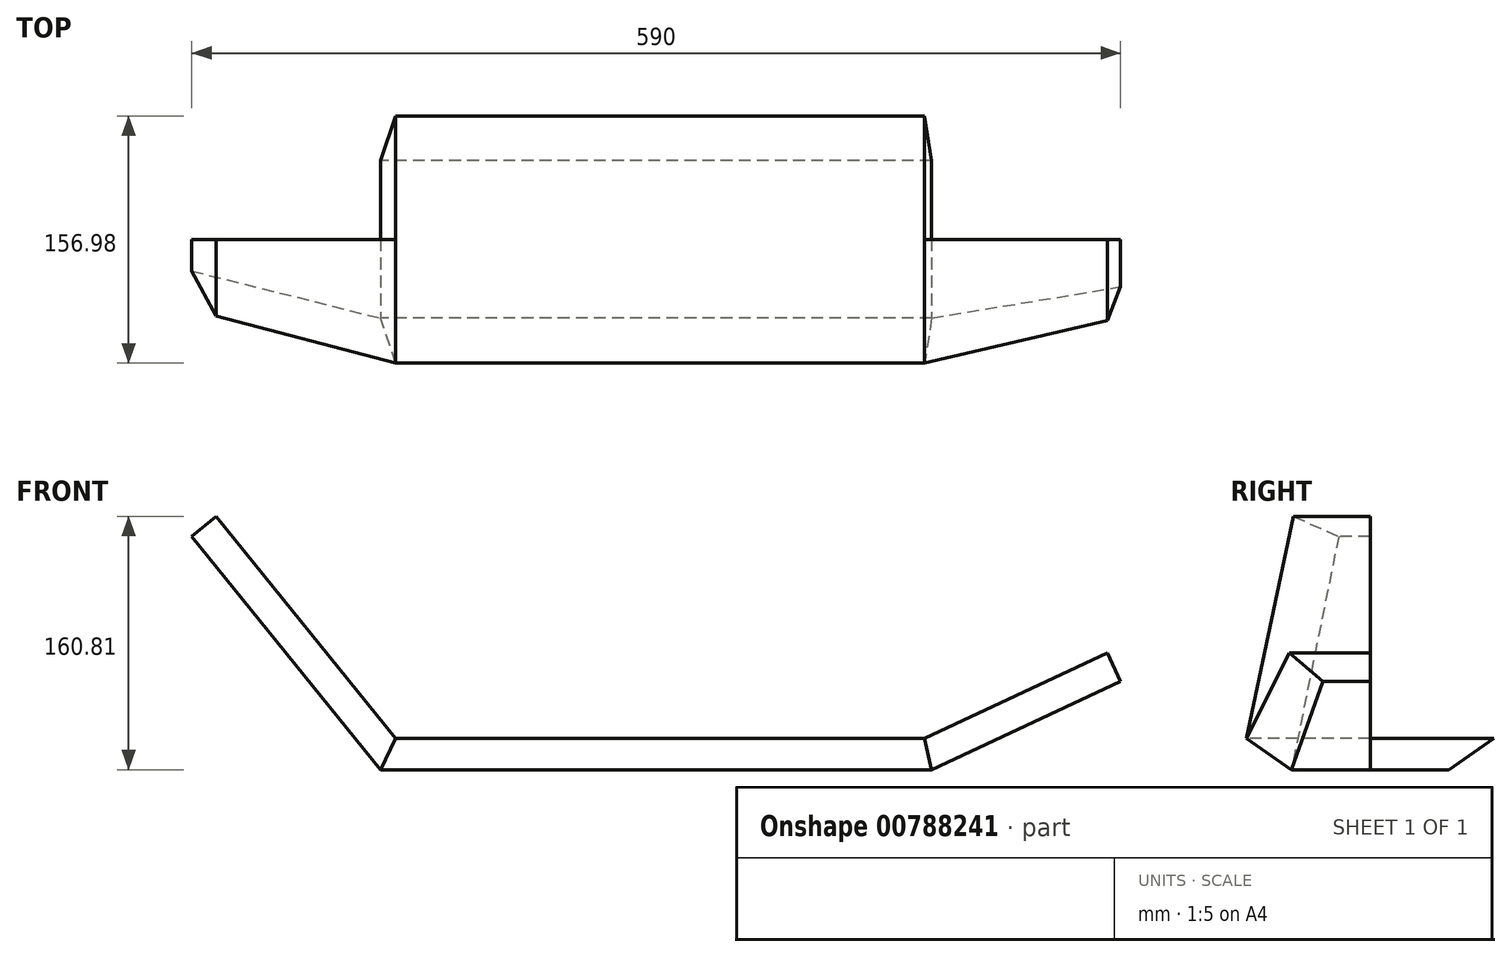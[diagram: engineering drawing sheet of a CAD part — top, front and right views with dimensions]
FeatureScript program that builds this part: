
annotation { "Feature Type Name" : "Feature", "Feature Type Description" : "" }
export const myFeature = defineFeature(function(context is Context, id is Id, definition is map)
    precondition{}
    {
        {
            var Q0;
            Q0=qCreatedBy(makeId("Front.planeOp"),FACE);
            var sketch = newSketch(context, id + "F0", { "sketchPlane" : qUnion([Q0])});
            skLineSegment(sketch, "E0", {"start": v(0, 0) * mm, "end": v(-200, 0) * mm});
            skLineSegment(sketch, "E1", {"start": v(-200, 0) * mm, "end": v(-320, 148.19) * mm});
            skLineSegment(sketch, "E2", {"start": v(0, 0) * mm, "end": v(150, 0) * mm});
            skLineSegment(sketch, "E3", {"start": v(150, 0) * mm, "end": v(270, 55.96) * mm});
            skLineSegment(sketch, "E4", {"start": v(-200, 0) * mm, "end": v(-320, 0) * mm, "construction": true});
            skLineSegment(sketch, "E5", {"start": v(-320, 0) * mm, "end": v(-320, 148.19) * mm, "construction": true});
            skLineSegment(sketch, "E6", {"start": v(150, 0) * mm, "end": v(270, 0) * mm, "construction": true});
            skLineSegment(sketch, "E7", {"start": v(270, 0) * mm, "end": v(270, 55.96) * mm, "construction": true});
            skLineSegment(sketch, "E8.0", {"start": v(-190.46, 20) * mm, "end": v(-304.46, 160.77) * mm});
            skLineSegment(sketch, "E8.1", {"start": v(0, 20) * mm, "end": v(-190.46, 20) * mm});
            skLineSegment(sketch, "E8.2", {"start": v(0, 20) * mm, "end": v(145.57, 20) * mm});
            skLineSegment(sketch, "E8.3", {"start": v(145.57, 20) * mm, "end": v(261.55, 74.08) * mm});
            skSolve(sketch);
        }
        {
            var Q0;
            Q0=sQuery(id+"F0.wireOp",EDGE,"E1");
            cPlane(context, id + "F1", {"entities" : qUnion([Q0]), "cplaneType" : CPlaneType.LINE_ANGLE, "offset" : 25 * mm, "angle" : 0 * degree, "width" : 150 * mm, "height" : 150 * mm});
        }
        {
            var Q0;
            Q0=qCreatedBy(id+"F1.planeOp",FACE);
            var sketch = newSketch(context, id + "F2", { "sketchPlane" : qUnion([Q0])});
            skPoint(sketch, "E9.end.orphan", {"position": v(0, 316.55) * mm});
            skLineSegment(sketch, "E10", {"start": v(0, 316.55) * mm, "end": v(-20, 316.55) * mm});
            skPoint(sketch, "E11.start.orphan", {"position": v(0, 117.6) * mm});
            skLineSegment(sketch, "E12", {"start": v(0, 125.86) * mm, "end": v(-50, 125.86) * mm});
            skLineSegment(sketch, "E13", {"start": v(-20, 316.55) * mm, "end": v(-50, 125.86) * mm});
            skLineSegment(sketch, "E14", {"start": v(0, 125.86) * mm, "end": v(0, 316.55) * mm});
            skSolve(sketch);
        }
        {
            var Q0;
            Q0=qCreatedBy(makeId("Top.planeOp"),FACE);
            var sketch = newSketch(context, id + "F3", { "sketchPlane" : qUnion([Q0])});
            skLineSegment(sketch, "E15", {"start": v(-200, -50) * mm, "end": v(150, -50) * mm});
            skLineSegment(sketch, "E16", {"start": v(150, -50) * mm, "end": v(150, 0) * mm});
            skLineSegment(sketch, "E17", {"start": v(-200, -50) * mm, "end": v(-200, 0) * mm});
            skLineSegment(sketch, "E18", {"start": v(-200, 0) * mm, "end": v(150, 0) * mm});
            skSolve(sketch);
        }
        {
            var Q0;
            Q0=sQuery(id+"F0.wireOp",EDGE,"E3");
            cPlane(context, id + "F4", {"entities" : qUnion([Q0]), "cplaneType" : CPlaneType.LINE_ANGLE, "offset" : 25 * mm, "angle" : 90 * degree, "width" : 150 * mm, "height" : 150 * mm});
        }
        {
            var Q0;
            Q0=qCreatedBy(id+"F4.planeOp",FACE);
            var sketch = newSketch(context, id + "F5", { "sketchPlane" : qUnion([Q0])});
            skLineSegment(sketch, "E19", {"start": v(268.35, 0) * mm, "end": v(268.35, -30) * mm});
            skLineSegment(sketch, "E20", {"start": v(135.95, 0) * mm, "end": v(135.95, -50) * mm});
            skLineSegment(sketch, "E21", {"start": v(135.95, -50) * mm, "end": v(268.35, -30) * mm});
            skLineSegment(sketch, "E22", {"start": v(135.95, 0) * mm, "end": v(268.35, 0) * mm});
            skSolve(sketch);
        }
        {
            var Q0;
            Q0=sQuery(id+"F0.wireOp",EDGE,"E8.0");
            cPlane(context, id + "F6", {"entities" : qUnion([Q0]), "cplaneType" : CPlaneType.LINE_ANGLE, "offset" : 25 * mm, "angle" : 0 * degree, "width" : 150 * mm, "height" : 150 * mm});
        }
        {
            var Q0;
            Q0=qCreatedBy(id+"F6.planeOp",FACE);
            var sketch = newSketch(context, id + "F7", { "sketchPlane" : qUnion([Q0])});
            skLineSegment(sketch, "E23", {"start": v(-48.79, 316.6) * mm, "end": v(-78.5, 135.4) * mm});
            skLineSegment(sketch, "E24", {"start": v(-78.5, 135.4) * mm, "end": v(0, 135.4) * mm});
            skLineSegment(sketch, "E25", {"start": v(0, 135.4) * mm, "end": v(0, 316.6) * mm});
            skLineSegment(sketch, "E26", {"start": v(0, 316.6) * mm, "end": v(-48.79, 316.6) * mm});
            skPoint(sketch, "E27.orphan", {"position": v(0, 341.24) * mm});
            skSolve(sketch);
        }
        {
            var Q0;
            Q0=sQuery(id+"F0.wireOp",EDGE,"E8.1");
            cPlane(context, id + "F8", {"entities" : qUnion([Q0]), "cplaneType" : CPlaneType.LINE_ANGLE, "offset" : 25 * mm, "angle" : 90 * degree, "width" : 150 * mm, "height" : 150 * mm});
        }
        {
            var Q0;
            Q0=qCreatedBy(id+"F8.planeOp",FACE);
            var sketch = newSketch(context, id + "F9", { "sketchPlane" : qUnion([Q0])});
            skLineSegment(sketch, "E28", {"start": v(-190.46, -78.5) * mm, "end": v(145.57, -78.5) * mm});
            skLineSegment(sketch, "E29", {"start": v(145.57, 0) * mm, "end": v(-190.46, 0) * mm});
            skLineSegment(sketch, "E30", {"start": v(-190.46, 0) * mm, "end": v(-190.46, -78.5) * mm});
            skLineSegment(sketch, "E31", {"start": v(145.57, 0) * mm, "end": v(145.57, -32.5) * mm});
            skLineSegment(sketch, "E32", {"start": v(145.57, -32.5) * mm, "end": v(145.57, -78.5) * mm});
            skPoint(sketch, "E33.orphan", {"position": v(162.28, 0) * mm});
            skSolve(sketch);
        }
        {
            var Q0;
            Q0=sQuery(id+"F0.wireOp",EDGE,"E8.3");
            cPlane(context, id + "F10", {"entities" : qUnion([Q0]), "cplaneType" : CPlaneType.LINE_ANGLE, "offset" : 25 * mm, "angle" : 90 * degree, "width" : 150 * mm, "height" : 150 * mm});
        }
        {
            var Q0;
            Q0=qCreatedBy(id+"F10.planeOp",FACE);
            var sketch = newSketch(context, id + "F11", { "sketchPlane" : qUnion([Q0])});
            skLineSegment(sketch, "E34", {"start": v(140.38, 0) * mm, "end": v(140.38, -78.5) * mm});
            skLineSegment(sketch, "E35", {"start": v(268.45, 0) * mm, "end": v(268.45, -51.46) * mm});
            skLineSegment(sketch, "E36", {"start": v(268.45, -51.46) * mm, "end": v(140.38, -78.5) * mm});
            skPoint(sketch, "E37.start.orphan", {"position": v(252.6, 0) * mm});
            skLineSegment(sketch, "E38", {"start": v(268.45, 0) * mm, "end": v(140.38, 0) * mm});
            skSolve(sketch);
        }
        {
            var Q0;
            Q0=makeQuery(id+"F5.imprint","IMPRINT",FACE,{"disambiguationData":[TD([[makeQuery(id+"F5.imprint","IMPRINT",EDGE,{"derivedFrom":sQuery(id+"F5.wireOp",EDGE,"E19")}),-1.0]])]});
            var Q1;
            Q1=makeQuery(id+"F11.imprint","IMPRINT",FACE,{"disambiguationData":[TD([[makeQuery(id+"F11.imprint","IMPRINT",EDGE,{"derivedFrom":sQuery(id+"F11.wireOp",EDGE,"E34")}),1.0]])]});
            loft(context, id + "F12", {"sheetProfilesArray" : [{ "sheetProfileEntities" : qUnion([Q0]) }, { "sheetProfileEntities" : qUnion([Q1]) }]});
        }
        {
            var Q0;
            Q0=makeQuery(id+"F7.imprint","IMPRINT",FACE,{"disambiguationData":[TD([[makeQuery(id+"F7.imprint","IMPRINT",EDGE,{"derivedFrom":sQuery(id+"F7.wireOp",EDGE,"E23")}),1.0]])]});
            var Q1;
            Q1=makeQuery(id+"F2.imprint","IMPRINT",FACE,{"disambiguationData":[TD([[makeQuery(id+"F2.imprint","IMPRINT",EDGE,{"derivedFrom":sQuery(id+"F2.wireOp",EDGE,"E10")}),1.0]])]});
            loft(context, id + "F13", {"sheetProfilesArray" : [{ "sheetProfileEntities" : qUnion([Q0]) }, { "sheetProfileEntities" : qUnion([Q1]) }]});
        }
        {
            var Q0;
            Q0=makeQuery(id+"F12.opLoft","SWEPT_FACE",FACE,{"disambiguationData":[OSD([sQuery(id+"F5.wireOp",EDGE,"E20"),sQuery(id+"F5.wireOp",EDGE,"E21"),sQuery(id+"F5.wireOp",EDGE,"E22"),sQuery(id+"F11.wireOp",EDGE,"E34"),sQuery(id+"F11.wireOp",EDGE,"E36"),sQuery(id+"F11.wireOp",EDGE,"E38")])]});
            var Q1;
            Q1=makeQuery(id+"F13.opLoft","SWEPT_FACE",FACE,{"disambiguationData":[OSD([sQuery(id+"F2.wireOp",EDGE,"E12"),sQuery(id+"F2.wireOp",EDGE,"E13"),sQuery(id+"F2.wireOp",EDGE,"E14"),sQuery(id+"F7.wireOp",EDGE,"E23"),sQuery(id+"F7.wireOp",EDGE,"E24"),sQuery(id+"F7.wireOp",EDGE,"E25")])]});
            loft(context, id + "F14", {"sheetProfilesArray" : [{ "sheetProfileEntities" : qUnion([Q0]) }, { "sheetProfileEntities" : qUnion([Q1]) }]});
        }
        {
            var Q0;
            Q0=makeQuery(id+"F14.opLoft","SWEPT_BODY",BODY,{"disambiguationData":[OSD([sQuery(id+"F2.wireOp",EDGE,"E12"),sQuery(id+"F2.wireOp",EDGE,"E13"),sQuery(id+"F2.wireOp",EDGE,"E14"),sQuery(id+"F5.wireOp",EDGE,"E20"),sQuery(id+"F5.wireOp",EDGE,"E21"),sQuery(id+"F5.wireOp",EDGE,"E22"),sQuery(id+"F7.wireOp",EDGE,"E23"),sQuery(id+"F7.wireOp",EDGE,"E24"),sQuery(id+"F7.wireOp",EDGE,"E25"),sQuery(id+"F11.wireOp",EDGE,"E34"),sQuery(id+"F11.wireOp",EDGE,"E36"),sQuery(id+"F11.wireOp",EDGE,"E38")])]});
            var Q1;
            Q1=qCreatedBy(makeId("Front.planeOp"),FACE);
            mirror(context, id + "F15", {"operationType" : NewBodyOperationType.ADD, "entities" : qUnion([Q0]), "mirrorPlane" : qUnion([Q1])});
        }
    });
